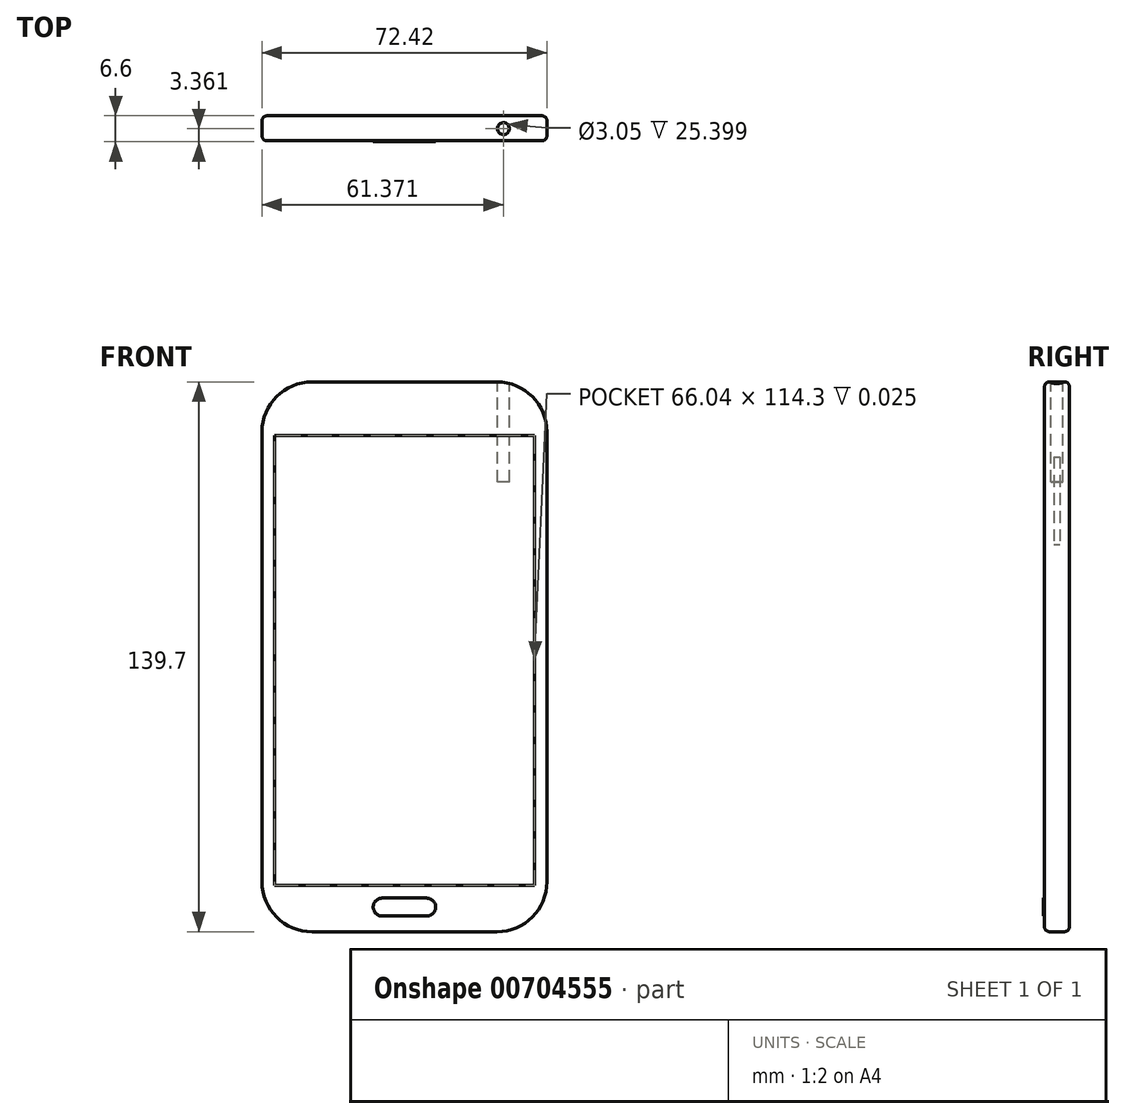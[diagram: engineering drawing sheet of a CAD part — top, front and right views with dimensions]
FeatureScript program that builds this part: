
annotation { "Feature Type Name" : "Feature", "Feature Type Description" : "" }
export const myFeature = defineFeature(function(context is Context, id is Id, definition is map)
    precondition{}
    {
        {
            var Q0;
            Q0=qCreatedBy(makeId("Front.planeOp"),FACE);
            var sketch = newSketch(context, id + "F0", { "sketchPlane" : qUnion([Q0])});
            skLineSegment(sketch, "E0.bottom", {"start": v(12.7, 0) * mm, "end": v(59.7, 0) * mm});
            skLineSegment(sketch, "E0.top", {"start": v(12.7, -139.7) * mm, "end": v(59.7, -139.7) * mm});
            skLineSegment(sketch, "E0.left", {"start": v(0, -12.7) * mm, "end": v(0, -127) * mm});
            skLineSegment(sketch, "E0.right", {"start": v(72.4, -12.7) * mm, "end": v(72.4, -127) * mm});
            skPoint(sketch, "E1.visualSharp", {"position": v(0, 0) * mm});
            skArc(sketch, "E1.filletArc", {"start": v(12.7, 0) * mm, "mid": v(3.72, -3.72) * mm, "end": v(0, -12.7) * mm});
            skPoint(sketch, "E2.visualSharp", {"position": v(72.4, 0) * mm});
            skArc(sketch, "E2.filletArc", {"start": v(72.4, -12.7) * mm, "mid": v(68.67, -3.72) * mm, "end": v(59.7, 0) * mm});
            skPoint(sketch, "E3.visualSharp", {"position": v(0, -139.7) * mm});
            skArc(sketch, "E3.filletArc", {"start": v(0, -127) * mm, "mid": v(3.72, -135.98) * mm, "end": v(12.7, -139.7) * mm});
            skPoint(sketch, "E4.visualSharp", {"position": v(72.4, -139.7) * mm});
            skArc(sketch, "E4.filletArc", {"start": v(59.7, -139.7) * mm, "mid": v(68.67, -135.98) * mm, "end": v(72.4, -127) * mm});
            skSolve(sketch);
        }
        {
            var Q0;
            Q0 = qSketchRegion(id + "F0", true);
            extrude(context, id + "F1", {"entities" : qUnion([Q0]), "depth" : 6.35 * mm, "offsetDistance" : 25.4 * mm});
        }
        {
            var Q0;
            Q0=makeQuery(id+"F1.opExtrude","CAP_FACE",FACE,{"disambiguationData":[OSD([sQuery(id+"F0.wireOp",EDGE,"E0.bottom"),sQuery(id+"F0.wireOp",EDGE,"E0.top"),sQuery(id+"F0.wireOp",EDGE,"E0.left"),sQuery(id+"F0.wireOp",EDGE,"E0.right"),sQuery(id+"F0.wireOp",EDGE,"E1.filletArc"),sQuery(id+"F0.wireOp",EDGE,"E2.filletArc"),sQuery(id+"F0.wireOp",EDGE,"E3.filletArc"),sQuery(id+"F0.wireOp",EDGE,"E4.filletArc")])],"isStart":false});
            var sketch = newSketch(context, id + "F2", { "sketchPlane" : qUnion([Q0])});
            skLineSegment(sketch, "E5", {"start": v(30.54, -131.17) * mm, "end": v(41.85, -131.17) * mm});
            skLineSegment(sketch, "E6", {"start": v(30.54, -135.74) * mm, "end": v(41.85, -135.74) * mm});
            skArc(sketch, "E7", {"start": v(30.54, -131.17) * mm, "mid": v(28.26, -133.45) * mm, "end": v(30.54, -135.74) * mm});
            skArc(sketch, "E8", {"start": v(41.85, -135.74) * mm, "mid": v(44.13, -133.45) * mm, "end": v(41.85, -131.17) * mm});
            skPoint(sketch, "E9", {"position": v(36.2, -131.17) * mm});
            skSolve(sketch);
        }
        {
            var Q0;
            Q0=makeQuery(id+"F2.imprint","IMPRINT",FACE,{"disambiguationData":[TD([[makeQuery(id+"F2.imprint","IMPRINT",EDGE,{"derivedFrom":sQuery(id+"F2.wireOp",EDGE,"E5")}),-1.0]])]});
            extrude(context, id + "F3", {"entities" : qUnion([Q0]), "operationType" : NewBodyOperationType.ADD, "depth" : 0.25 * mm, "offsetDistance" : 25.4 * mm});
        }
        {
            var Q0;
            Q0=makeQuery(id+"F1.opExtrude","CAP_EDGE",EDGE,{"disambiguationData":[OSD([sQuery(id+"F0.wireOp",EDGE,"E0.right")])],"isStart":false});
            var Q1;
            Q1=makeQuery(id+"F1.opExtrude","CAP_EDGE",EDGE,{"disambiguationData":[OSD([sQuery(id+"F0.wireOp",EDGE,"E0.right")])],"isStart":true});
            fillet(context, id + "F4", {"entities" : qUnion([Q0, Q1]), "radius" : 1.27 * mm, "tangentPropagation" : true, "allowEdgeOverflow" : false});
        }
        {
            var Q0;
            Q0=makeQuery(id+"F1.opExtrude","CAP_FACE",FACE,{"disambiguationData":[OSD([sQuery(id+"F0.wireOp",EDGE,"E0.bottom"),sQuery(id+"F0.wireOp",EDGE,"E0.top"),sQuery(id+"F0.wireOp",EDGE,"E0.left"),sQuery(id+"F0.wireOp",EDGE,"E0.right"),sQuery(id+"F0.wireOp",EDGE,"E1.filletArc"),sQuery(id+"F0.wireOp",EDGE,"E2.filletArc"),sQuery(id+"F0.wireOp",EDGE,"E3.filletArc"),sQuery(id+"F0.wireOp",EDGE,"E4.filletArc")])],"isStart":false});
            var sketch = newSketch(context, id + "F5", { "sketchPlane" : qUnion([Q0])});
            skLineSegment(sketch, "E10.bottom", {"start": v(3.17, -13.7) * mm, "end": v(69.22, -13.7) * mm});
            skLineSegment(sketch, "E10.top", {"start": v(3.17, -128) * mm, "end": v(69.22, -128) * mm});
            skLineSegment(sketch, "E10.left", {"start": v(3.17, -13.7) * mm, "end": v(3.18, -128) * mm});
            skLineSegment(sketch, "E10.right", {"start": v(69.22, -13.7) * mm, "end": v(69.22, -128) * mm});
            skPoint(sketch, "E11", {"position": v(36.2, -13.7) * mm});
            skPoint(sketch, "E12", {"position": v(36.2, -128) * mm});
            skSolve(sketch);
        }
        {
            var Q0;
            Q0=makeQuery(id+"F5.imprint","IMPRINT",FACE,{"disambiguationData":[TD([[makeQuery(id+"F5.imprint","IMPRINT",EDGE,{"derivedFrom":sQuery(id+"F5.wireOp",EDGE,"E10.bottom")}),-1.0]])]});
            extrude(context, id + "F6", {"entities" : qUnion([Q0]), "operationType" : NewBodyOperationType.REMOVE, "oppositeDirection" : true, "depth" : 0.03 * mm, "offsetDistance" : 25.4 * mm});
        }
        {
            var Q0;
            Q0=makeQuery(id+"F1.opExtrude","SWEPT_FACE",FACE,{"disambiguationData":[OSD([sQuery(id+"F0.wireOp",EDGE,"E0.left")])]});
            cPlane(context, id + "F7", {"entities" : qUnion([Q0]), "cplaneType" : CPlaneType.OFFSET, "offset" : 0 * mm, "width" : 152.4 * mm, "height" : 152.4 * mm});
        }
        {
            var Q0;
            Q0=qCreatedBy(id+"F7.planeOp",FACE);
            var sketch = newSketch(context, id + "F8", { "sketchPlane" : qUnion([Q0])});
            skLineSegment(sketch, "E13.bottom", {"start": v(3.99, -19.05) * mm, "end": v(2.4, -19.05) * mm});
            skLineSegment(sketch, "E13.top", {"start": v(3.99, -41.28) * mm, "end": v(2.4, -41.28) * mm});
            skLineSegment(sketch, "E13.left", {"start": v(3.99, -19.05) * mm, "end": v(3.99, -41.28) * mm});
            skLineSegment(sketch, "E13.right", {"start": v(2.4, -19.05) * mm, "end": v(2.4, -41.28) * mm});
            skSolve(sketch);
        }
        {
            var Q0;
            Q0=makeQuery(id+"F8.imprint","IMPRINT",FACE,{"disambiguationData":[TD([[makeQuery(id+"F8.imprint","IMPRINT",EDGE,{"derivedFrom":sQuery(id+"F8.wireOp",EDGE,"E13.bottom")}),1.0]])]});
            extrude(context, id + "F9", {"entities" : qUnion([Q0]), "operationType" : NewBodyOperationType.ADD, "depth" : 0.03 * mm, "offsetDistance" : 25.4 * mm});
        }
        {
            var Q0;
            Q0=makeQuery(id+"F1.opExtrude","SWEPT_FACE",FACE,{"disambiguationData":[OSD([sQuery(id+"F0.wireOp",EDGE,"E0.bottom")])]});
            cPlane(context, id + "F10", {"entities" : qUnion([Q0]), "cplaneType" : CPlaneType.OFFSET, "offset" : 0 * mm, "width" : 152.4 * mm, "height" : 152.4 * mm});
        }
        {
            var Q0;
            Q0=qCreatedBy(id+"F10.planeOp",FACE);
            var sketch = newSketch(context, id + "F11", { "sketchPlane" : qUnion([Q0])});
            skCircle(sketch, "E14", {"center": v(61.34, -3.24) * mm, "radius": 1.52 * mm});
            skSolve(sketch);
        }
        {
            var Q0;
            Q0=makeQuery(id+"F11.imprint","IMPRINT",FACE,{"disambiguationData":[TD([[makeQuery(id+"F11.imprint","IMPRINT",EDGE,{"derivedFrom":sQuery(id+"F11.wireOp",EDGE,"E14")}),1.0]])]});
            extrude(context, id + "F12", {"entities" : qUnion([Q0]), "operationType" : NewBodyOperationType.REMOVE, "oppositeDirection" : true, "depth" : 25.4 * mm, "offsetDistance" : 25.4 * mm});
        }
    });
